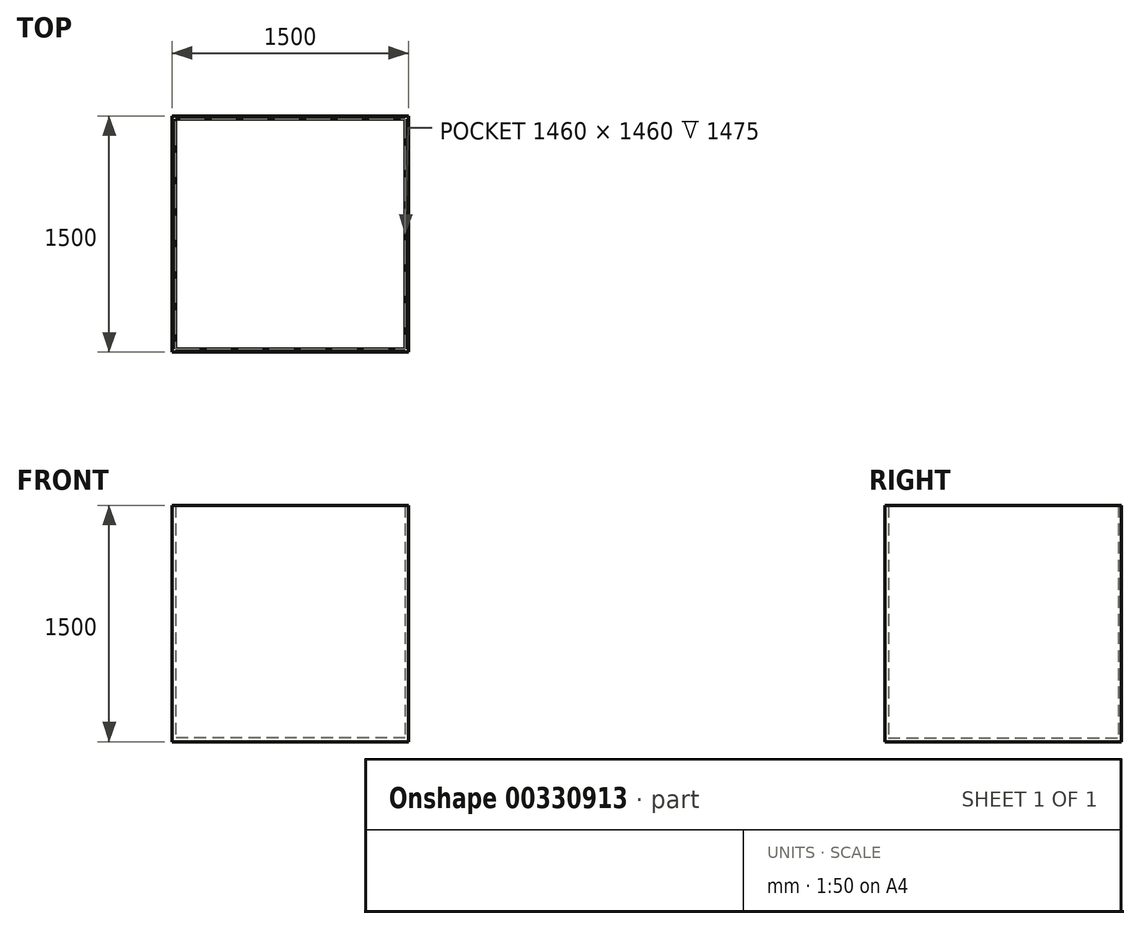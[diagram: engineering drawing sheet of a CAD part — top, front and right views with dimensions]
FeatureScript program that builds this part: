
annotation { "Feature Type Name" : "Feature", "Feature Type Description" : "" }
export const myFeature = defineFeature(function(context is Context, id is Id, definition is map)
    precondition{}
    {
        {
            var Q0;
            Q0=qCreatedBy(makeId("Top.planeOp"),FACE);
            var sketch = newSketch(context, id + "F0", { "sketchPlane" : qUnion([Q0])});
            skLineSegment(sketch, "E0.bottom", {"start": v(-750, 750) * mm, "end": v(750, 750) * mm});
            skLineSegment(sketch, "E0.top", {"start": v(-750, -750) * mm, "end": v(750, -750) * mm});
            skLineSegment(sketch, "E0.left", {"start": v(-750, 750) * mm, "end": v(-750, -750) * mm});
            skLineSegment(sketch, "E0.right", {"start": v(750, 750) * mm, "end": v(750, -750) * mm});
            skPoint(sketch, "E0.middle", {"position": v(0, 0) * mm});
            skLineSegment(sketch, "E1.0", {"start": v(730, 730) * mm, "end": v(730, -730) * mm});
            skLineSegment(sketch, "E1.1", {"start": v(-730, 730) * mm, "end": v(730, 730) * mm});
            skLineSegment(sketch, "E1.2", {"start": v(-730, 730) * mm, "end": v(-730, -730) * mm});
            skLineSegment(sketch, "E1.3", {"start": v(-730, -730) * mm, "end": v(730, -730) * mm});
            skSolve(sketch);
        }
        {
            var Q0;
            Q0=qSketchRegion(id+"F0",true);
            extrude(context, id + "F1", {"entities" : qUnion([Q0]), "depth" : 1500 * mm});
        }
        {
            var Q0;
            Q0=makeQuery(id+"F1.opExtrude","CAP_FACE",FACE,{"disambiguationData":[OSD([sQuery(id+"F0.wireOp",EDGE,"E0.bottom"),sQuery(id+"F0.wireOp",EDGE,"E0.top"),sQuery(id+"F0.wireOp",EDGE,"E0.left"),sQuery(id+"F0.wireOp",EDGE,"E0.right"),sQuery(id+"F0.wireOp",EDGE,"E1.0"),sQuery(id+"F0.wireOp",EDGE,"E1.1"),sQuery(id+"F0.wireOp",EDGE,"E1.2"),sQuery(id+"F0.wireOp",EDGE,"E1.3")])],"isStart":true});
            var sketch = newSketch(context, id + "F2", { "sketchPlane" : qUnion([Q0])});
            skLineSegment(sketch, "E2.0", {"start": v(750, -750) * mm, "end": v(750, 750) * mm});
            skLineSegment(sketch, "E2.1", {"start": v(-750, -750) * mm, "end": v(-750, 750) * mm});
            skLineSegment(sketch, "E2.2", {"start": v(-750, -750) * mm, "end": v(750, -750) * mm});
            skLineSegment(sketch, "E2.3", {"start": v(-750, 750) * mm, "end": v(750, 750) * mm});
            skSolve(sketch);
        }
        {
            var Q0;
            Q0=qSketchRegion(id+"F2",true);
            extrude(context, id + "F3", {"entities" : qUnion([Q0]), "operationType" : NewBodyOperationType.ADD, "oppositeDirection" : true, "depth" : 25 * mm});
        }
    });
